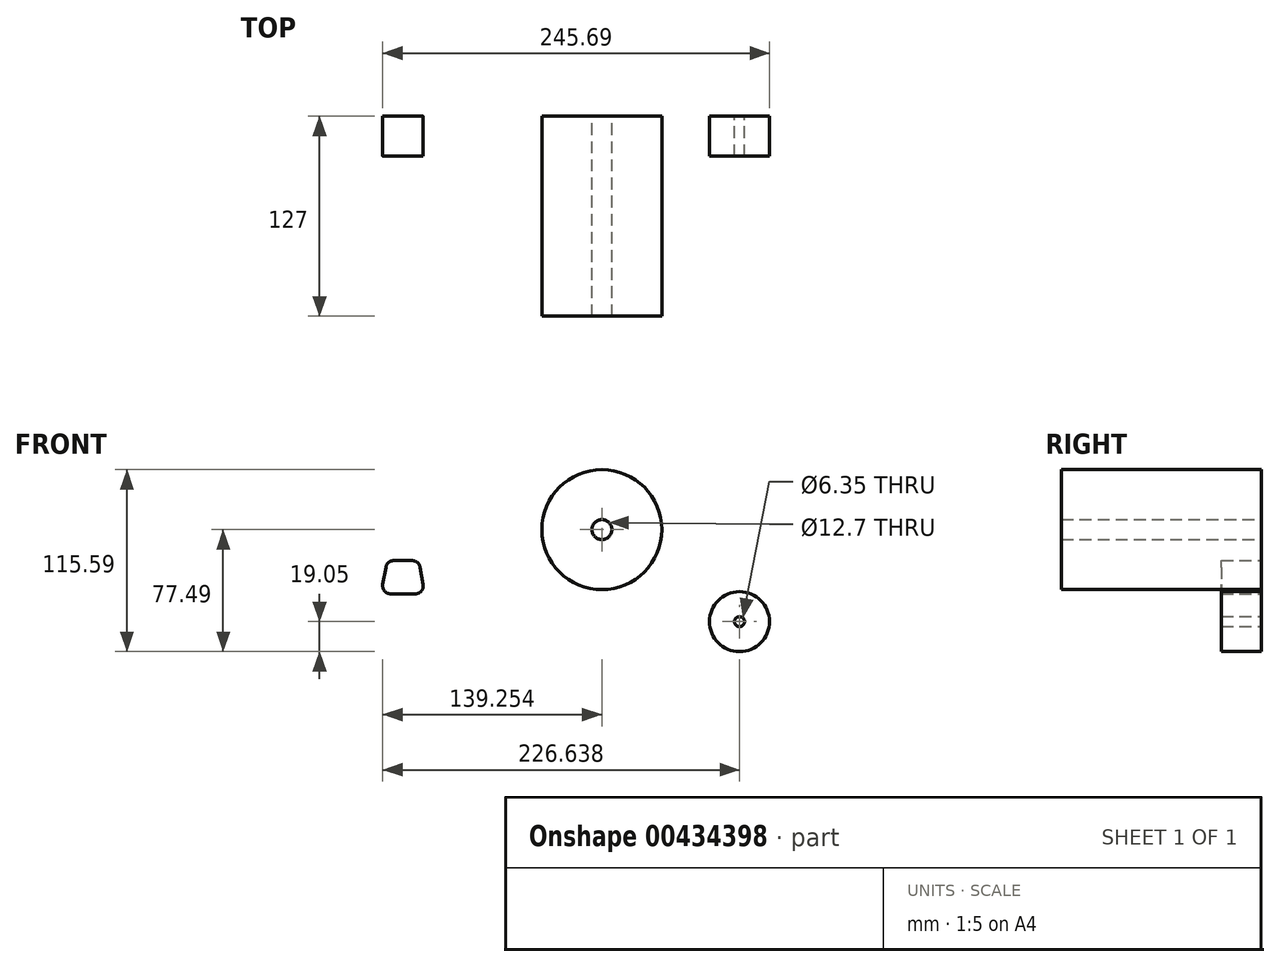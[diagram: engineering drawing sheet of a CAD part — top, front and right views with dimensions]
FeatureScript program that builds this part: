
annotation { "Feature Type Name" : "Feature", "Feature Type Description" : "" }
export const myFeature = defineFeature(function(context is Context, id is Id, definition is map)
    precondition{}
    {
        {
            var Q0;
            Q0=qCreatedBy(makeId("Front.planeOp"),FACE);
            var sketch = newSketch(context, id + "F0", { "sketchPlane" : qUnion([Q0])});
            skCircle(sketch, "E0", {"center": v(-54.02, 27.1) * mm, "radius": 38.1 * mm});
            skCircle(sketch, "E1", {"center": v(-54.02, 27.1) * mm, "radius": 6.35 * mm});
            skSolve(sketch);
        }
        {
            var Q0;
            Q0 = qSketchRegion(id + "F0", true);
            extrude(context, id + "F1", {"entities" : qUnion([Q0]), "depth" : 127 * mm});
        }
        {
            var Q0;
            Q0 = qSketchRegion(id + "F0", true);
            extrude(context, id + "F2", {"entities" : qUnion([Q0]), "operationType" : NewBodyOperationType.ADD, "depth" : 12.7 * mm});
        }
        {
            var Q0;
            Q0=qCreatedBy(makeId("Front.planeOp"),FACE);
            var sketch = newSketch(context, id + "F3", { "sketchPlane" : qUnion([Q0])});
            skCircle(sketch, "E2", {"center": v(33.37, -31.34) * mm, "radius": 19.05 * mm});
            skCircle(sketch, "E3", {"center": v(33.37, -31.34) * mm, "radius": 3.18 * mm});
            skLineSegment(sketch, "E4", {"start": v(-186.26, 7.4) * mm, "end": v(-174.5, 7.4) * mm});
            skLineSegment(sketch, "E5", {"start": v(-169.5, 3.2) * mm, "end": v(-167.56, -7.76) * mm});
            skLineSegment(sketch, "E6", {"start": v(-191.26, 3.2) * mm, "end": v(-193.2, -7.76) * mm});
            skLineSegment(sketch, "E7", {"start": v(-188.2, -13.72) * mm, "end": v(-172.56, -13.72) * mm});
            skPoint(sketch, "E8.visualSharp", {"position": v(-190.52, 7.4) * mm});
            skArc(sketch, "E8.filletArc", {"start": v(-186.26, 7.4) * mm, "mid": v(-189.53, 6.2) * mm, "end": v(-191.26, 3.2) * mm});
            skPoint(sketch, "E9.visualSharp", {"position": v(-170.23, 7.4) * mm});
            skArc(sketch, "E9.filletArc", {"start": v(-169.5, 3.2) * mm, "mid": v(-171.23, 6.2) * mm, "end": v(-174.5, 7.4) * mm});
            skPoint(sketch, "E10.visualSharp", {"position": v(-166.5, -13.72) * mm});
            skArc(sketch, "E10.filletArc", {"start": v(-172.56, -13.72) * mm, "mid": v(-168.67, -11.9) * mm, "end": v(-167.56, -7.76) * mm});
            skPoint(sketch, "E11.visualSharp", {"position": v(-194.25, -13.72) * mm});
            skArc(sketch, "E11.filletArc", {"start": v(-193.2, -7.76) * mm, "mid": v(-192.08, -11.9) * mm, "end": v(-188.2, -13.72) * mm});
            skSolve(sketch);
        }
        {
            var Q0;
            Q0 = qSketchRegion(id + "F3", true);
            extrude(context, id + "F4", {"entities" : qUnion([Q0]), "depth" : 25.4 * mm});
        }
    });
